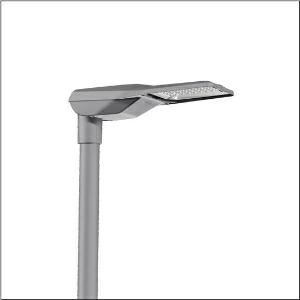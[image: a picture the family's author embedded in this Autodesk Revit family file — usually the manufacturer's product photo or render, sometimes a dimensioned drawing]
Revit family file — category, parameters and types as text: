
# Revit family: streetlight_sl_21_iq_mini___stw1_0a_5xe2e41d08jb_35ba
name_source: partatom
category: Lighting Fixtures
units: mm (PartAtom-declared; Revit-internal decimal feet)

## family parameters
Cut with Voids When Loaded = No
Host = Face
Light Source = No
Part Type = Normal
Room Calculation Point = No
Round Connector Dimension = Use Diameter
Shared = No

## types (1)
- --- (1 x LED, 11290 lm, 71.6 W, 4000K)
    Apparent Load = 72 VA
    CIE Flux Codes = 39 75 98 100 100
    Color Rendering = 70
    Color Temperature = 4000K
    Default Elevation = 1800 mm
    Description = Streetlight SL 21 iQ mini, mast luminaire, primary light control with lens, of PMMA, primary optical cover: cover, of toughened safety glass, transparent, light distribution: STW1.0a, light emission: direct distribution, primary light characteristic: asymmetric, installation type: post-top, side-entry, LED, High Power LED, rated luminous flux: 11.290lm, luminous efficacy: 158lm/W, light colour: 740, colour temperature: 4000K, control: Auto-Match, Temp-Guard, Lumen-Switch, Night-Set, Smart-Wire, Light-Fading, Desk-Remote (wireless, voltage-free reading and setting of iQ features in the workshop via application-optimized NFC function/RFID function), optimised constant luminous flux control (CLO 2.0), presetting dimming linear, mains connection: 220..240V, AC, 50/60Hz, start of lifetime: 72W, end of service life: 75W, reduction: 33W, luminaire housing, of diecast aluminium, powder-coated, Siteco® metallic grey (DB 702S), corrosivity category C5 mid according to DIN EN ISO 12944, please order mast flange separately, inclination adjustable: 0°, 5°, 10°, 15°, sealing non-destructively replaceable, multi-level sealing system, length: 628mm, width: 235mm, height: 110mm, mast flange for spigot size: 42mm (side-entry): 5XC10008XM4, 60/48mm (side-entry/post-top): 5XC10108XM2, 76/60mm (side-entry/post-top): 5XC10108XM1, protection rating (complete): IP66, insulation class (complete): insulation class II (safety insulation), certification: CE, ENEC, ENEC+, VDE, impact resistance: IK09, permissible operating ambient temperature for outdoor applications: -40..+50°C, standard-compliant lighting for roads and squares, packaging unit: 1 piece

Light Distribution: STW1.0a
    Height = 110 mm
    Lamp = 1 x LED
    Lamp Light Flux = 11290 lm
    Lamp Power = 71.6 W
    Lamp count = 1
    Length = 625 mm
    Luminous efficacy = 158 lm/W
    Manufacturer = Siteco
    ModVariant = No
    Model = 5XE2E41D08JB
    Number of Poles = 1
    OnlyDefault = Yes
    Power Factor = 1
    Product Name = Streetlight SL 21 iQ mini | STW1.0a
    Product group = mast luminaire | pylon top
    ProductGroupID = 6100
    Protection Class = Protection class II
    Protection Degree = IP 66
    RLX_Detail_Level = 1
    RLX_Emergency_Light_Flux = 0 lm
    RLX_Emergency_Type = 0
    RLX_Emergency_Type_DB = No
    RlxData = <blob elided: 92021 chars, md5=ad33b3a3>
    Socket = socket
    Standby Power = 0 W
    System Light Flux = 11290 lm
    System Power = 72 W
    Type Comments = factory setting: luminous flux: 100 % | dim-lin: 254 | 746 mA
    Type Image = l_1003519.jpg
    URL = http://relux.com
    VarID = @adj_120743
    Voltage = 0 V
    Weight = 0.00 kg
    Width = 234 mm

## geometry (parser evidence)
native form markers: Blend x4, Sweep x13
no freeform markers — native parametric forms only
